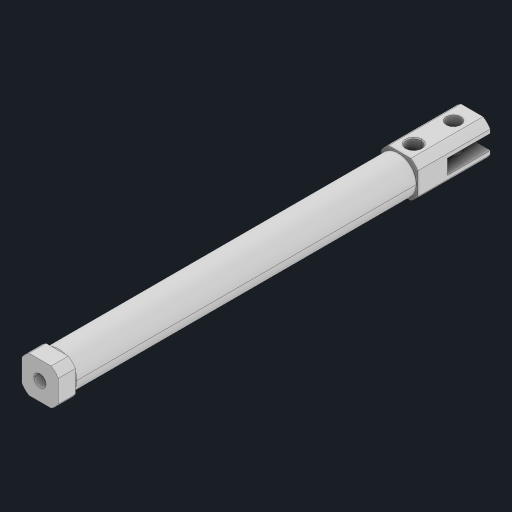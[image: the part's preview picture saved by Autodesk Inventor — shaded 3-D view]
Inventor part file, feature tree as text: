
AUTODESK INVENTOR PART (.ipt)
format: ipt  version: 2023 (Build 270158030, 158C)  size: 138,240 bytes
history: native  units: in
note: dims shown in document units (in); Inventor stores cm internally (conversion verified against a paired STEP export)
features: extrude x2, sketch x2, imported_body x1
ambient origin geometry x8: Origin, YZ Plane, XZ Plane, XY Plane, X Axis, Y Axis, Z Axis, Center Point
bodies: Solid1 (feature_tree)
feature tree (5):
  extrude  "Extrusion1"  TaperAngle=0.0deg  [1 undecoded]
  extrude  "Extrusion2"  [1 undecoded]
  sketch  "Sketch1"  dims[d0=0.0in d1=0.0in d2=0.0in d3=0.0in]
  sketch  "Sketch2"
  imported_body  "Base1"
note: 2 required parameter values undecoded (feature->parameter linkage not recoverable at this tier; creation-order binding heuristic only, values carry confidence <= 0.55)
